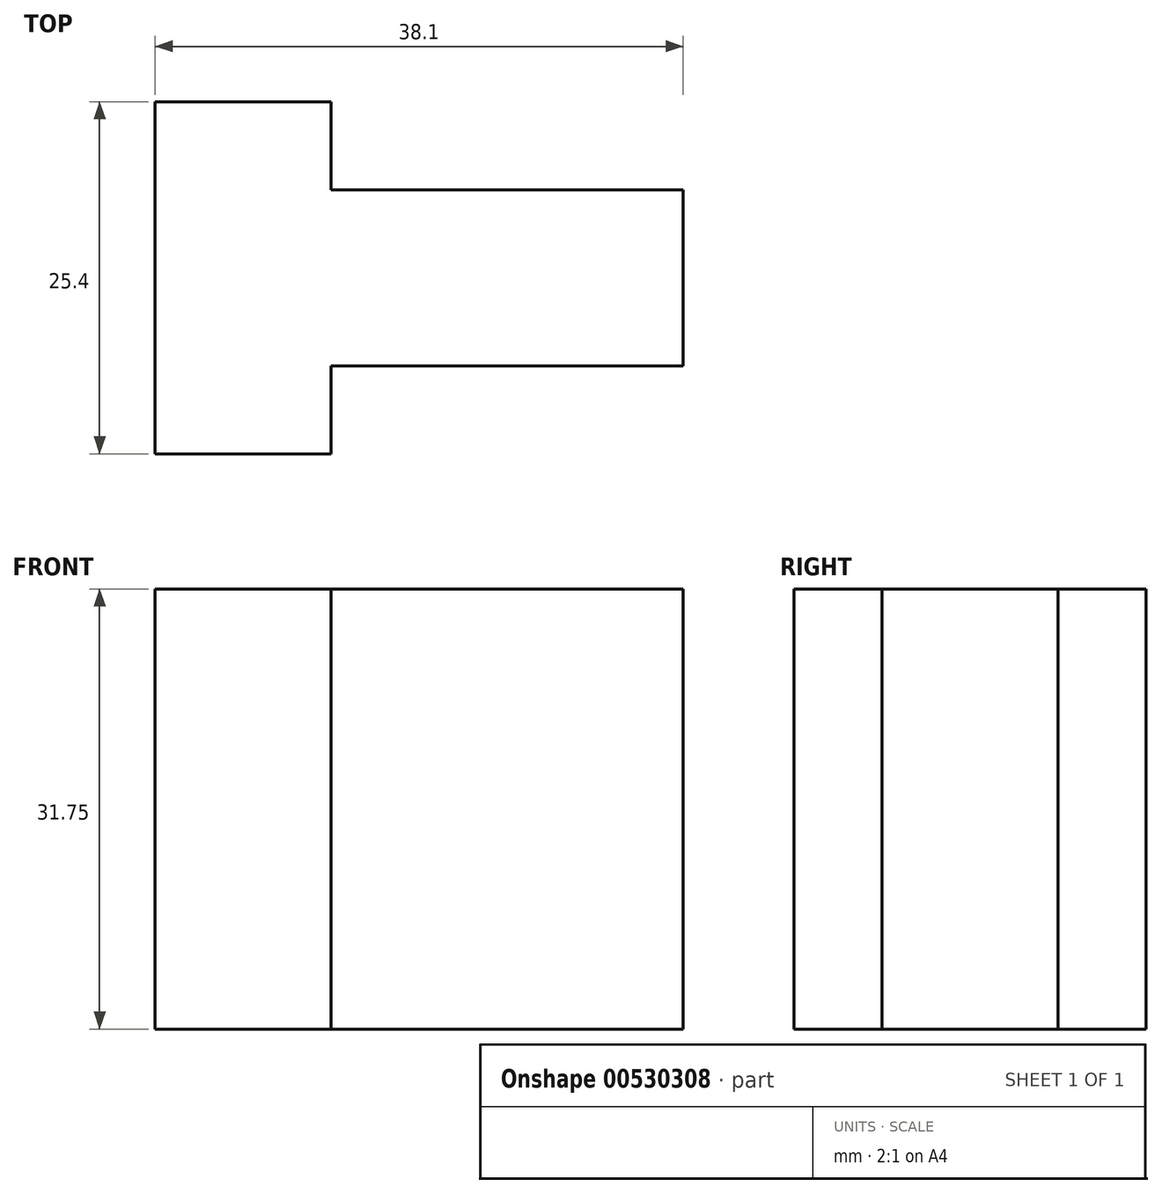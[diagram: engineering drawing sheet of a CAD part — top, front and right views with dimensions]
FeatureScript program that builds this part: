
annotation { "Feature Type Name" : "Feature", "Feature Type Description" : "" }
export const myFeature = defineFeature(function(context is Context, id is Id, definition is map)
    precondition{}
    {
        {
            var Q0;
            Q0=qCreatedBy(makeId("Front.planeOp"),FACE);
            var sketch = newSketch(context, id + "F0", { "sketchPlane" : qUnion([Q0])});
            skLineSegment(sketch, "E0", {"start": v(-55.58, 45.1) * mm, "end": v(-55.58, 13.35) * mm});
            skLineSegment(sketch, "E1", {"start": v(-55.58, 13.35) * mm, "end": v(-17.48, 13.35) * mm});
            skLineSegment(sketch, "E2", {"start": v(-17.48, 13.35) * mm, "end": v(-17.48, 45.1) * mm});
            skLineSegment(sketch, "E3", {"start": v(-17.48, 45.1) * mm, "end": v(-55.58, 45.1) * mm});
            skSolve(sketch);
        }
        {
            var Q0;
            Q0=makeQuery(id+"F0.imprint","IMPRINT",FACE,{"disambiguationData":[TD([[makeQuery(id+"F0.imprint","IMPRINT",EDGE,{"derivedFrom":sQuery(id+"F0.wireOp",EDGE,"E0")}),1.0]])]});
            extrude(context, id + "F1", {"entities" : qUnion([Q0]), "depth" : 25.4 * mm, "offsetDistance" : 25.4 * mm});
        }
        {
            var Q0;
            Q0=makeQuery(id+"F1.opExtrude","SWEPT_FACE",FACE,{"disambiguationData":[OSD([sQuery(id+"F0.wireOp",EDGE,"E3")])]});
            var sketch = newSketch(context, id + "F2", { "sketchPlane" : qUnion([Q0])});
            skLineSegment(sketch, "E4", {"start": v(-42.88, 0) * mm, "end": v(-42.88, -6.35) * mm});
            skLineSegment(sketch, "E5", {"start": v(-42.88, -6.35) * mm, "end": v(-17.48, -6.35) * mm});
            skLineSegment(sketch, "E6", {"start": v(-17.48, -6.35) * mm, "end": v(-17.48, -19.05) * mm});
            skLineSegment(sketch, "E7", {"start": v(-17.48, -19.05) * mm, "end": v(-42.88, -19.05) * mm});
            skLineSegment(sketch, "E8", {"start": v(-42.88, -19.05) * mm, "end": v(-42.88, -25.4) * mm});
            skSolve(sketch);
        }
        {
            var Q0;
            {var subQ0=sQuery(id+"F2.wireOp",EDGE,"E4");Q0=makeQuery(id+"F2.imprint","IMPRINT",FACE,{"disambiguationData":[TD([[makeQuery(id+"F2.imprint","IMPRINT",EDGE,{"derivedFrom":subQ0}),1.0]])]});}
            var Q1;
            {var subQ0=sQuery(id+"F2.wireOp",EDGE,"E7");Q1=makeQuery(id+"F2.imprint","IMPRINT",FACE,{"disambiguationData":[TD([[makeQuery(id+"F2.imprint","IMPRINT",EDGE,{"derivedFrom":subQ0}),1.0]])]});}
            extrude(context, id + "F3", {"entities" : qUnion([Q0, Q1]), "operationType" : NewBodyOperationType.REMOVE, "endBound" : BoundingType.THROUGH_ALL, "oppositeDirection" : true, "depth" : 25.4 * mm, "offsetDistance" : 25.4 * mm});
        }
    });
